# Revit family: Reece_Toilet_Roca_The Gap_Wall Hung_Rimless_P trap
name_source: partatom
category: Plumbing Fixtures
revit_build: Autodesk Revit 2018 (Build: 20190510_1515(x64)
units: mm (PartAtom-declared; Revit-internal decimal feet)

## family parameters
Always vertical = Yes
Cut with Voids When Loaded = No
Part Type = Normal
Room Calculation Point = No
Round Connector Dimension = Use Diameter
Shared = No
Work Plane-Based = No

## types (1)
- Vitreous China_White
    Description = Roca The Gap Rimless Wall Hung Pan Soft Close Quick Release Toilet Set White (4 Star)
    Disclaimer = THIS FILE IS THE PROPERTY OF THE REECE GROUP. IT MAY NOT BE REPRODUCED, REVERSE-ENGINEERED OR MODIFIED. ANY REPUBLICATION, TRANSMISSION OR DISTRIBUTION FOR THE PURPOSE OF COMMERCIALLY EXPLOITING THE FILES IS PROHIBITED.
    Keynote = Product #9509110, Reece_Toilet_Roca_The Gap_Wall Hung_Rimless_P trap - Vitreous China_White
    Manufacturer = Roca
    Model = The Gap
    Reece_Back_Inlet = 55 mm  [stored 0.180446 ft]
    Reece_Back_Outlet_Offset = 220 mm  [stored 0.721785 ft]
    Reece_Detail_Disclaimer = THIS FILE IS THE PROPERTY OF THE REECE GROUP. IT MAY NOT BE REPRODUCED, REVERSE-ENGINEERED OR MODIFIED. ANY REPUBLICATION, TRANSMISSION OR DISTRIBUTION FOR THE PURPOSE OF COMMERCIALLY EXPLOITING THE FILES IS PROHIBITED.
    Reece_Detail_Function = P trap
    Reece_Detail_Installation = Pan Wall Hung
    Reece_Detail_Shape = Rimless
    Reece_Material_Main = Reece_Vitreous China_White
    Reece_Material_Seat = Reece_Vitreous China_White
    Reece_Overall_Projection = 540 mm  [stored 1.77165 ft]
    Reece_Overall_Width = 350 mm  [stored 1.14829 ft]
    Reece_P_Trap = 102 mm
    Reece_Pan_Height = 400 mm  [stored 1.31234 ft]
    Reece_Product_Brand = Roca
    Reece_Product_Description = Roca The Gap Rimless Wall Hung Pan Soft Close Quick Release Toilet Set White (4 Star)
    Reece_Product_Mount = Wall Mounted
    Reece_Product_Number = 9509110
    Reece_Product_Sub Brand = The Gap
    Reece_Product_Web Page = https://www.reece.com.au
    URL = https://www.reece.com.au

note: [stored X ft] marks values corroborated as IEEE doubles in the binary element streams (Revit-internal decimal feet)

## geometry (parser evidence)
native form markers: Sweep x7
no freeform markers — native parametric forms only
